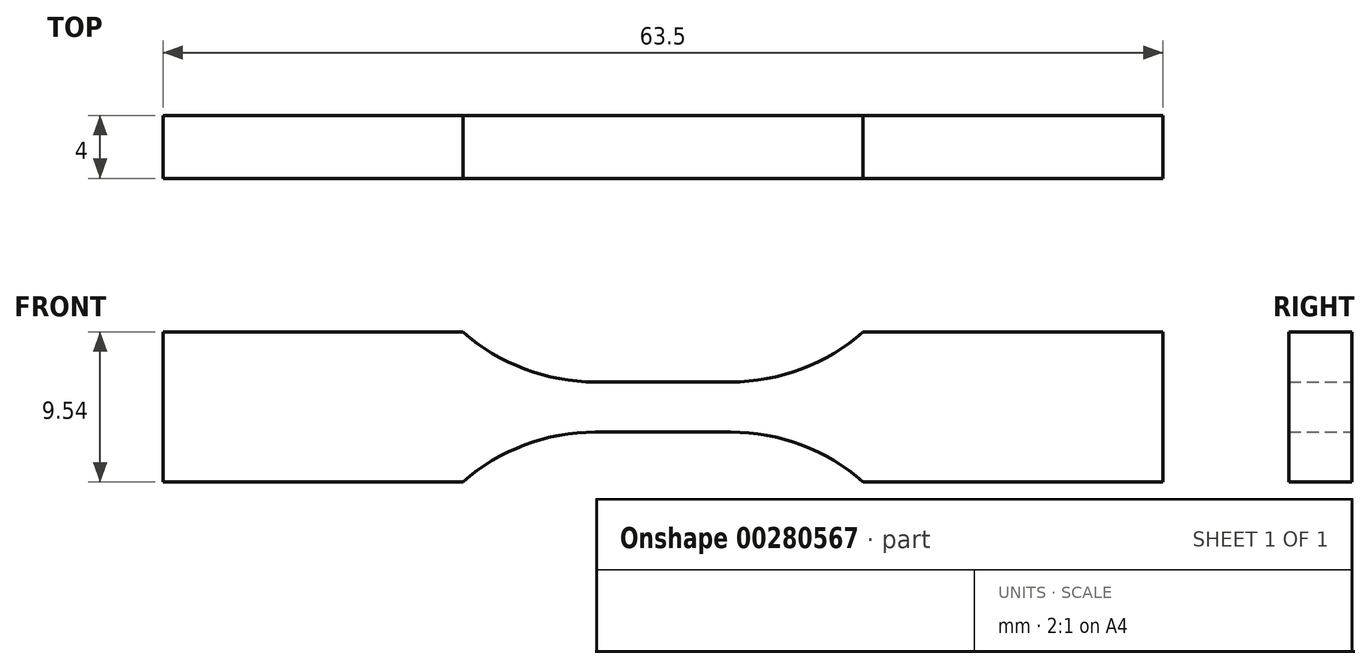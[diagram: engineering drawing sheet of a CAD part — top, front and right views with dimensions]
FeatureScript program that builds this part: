
annotation { "Feature Type Name" : "Feature", "Feature Type Description" : "" }
export const myFeature = defineFeature(function(context is Context, id is Id, definition is map)
    precondition{}
    {
        {
            var Q0;
            Q0=qCreatedBy(makeId("Front.planeOp"),FACE);
            var sketch = newSketch(context, id + "F0", { "sketchPlane" : qUnion([Q0])});
            skLineSegment(sketch, "E0", {"start": v(0, 1.6) * mm, "end": v(4.3, 1.6) * mm});
            skArc(sketch, "E1", {"start": v(4.3, 1.6) * mm, "mid": v(8.79, 2.41) * mm, "end": v(12.7, 4.76) * mm});
            skLineSegment(sketch, "E2", {"start": v(12.7, 4.77) * mm, "end": v(31.75, 4.77) * mm});
            skLineSegment(sketch, "E3", {"start": v(31.75, 4.77) * mm, "end": v(31.75, 0) * mm});
            skLineSegment(sketch, "E4.MirrorCS", {"start": v(0, -1.6) * mm, "end": v(4.3, -1.6) * mm});
            skLineSegment(sketch, "E5.MirrorCS", {"start": v(31.75, -4.77) * mm, "end": v(31.75, 0) * mm});
            skLineSegment(sketch, "E6.MirrorCS", {"start": v(12.7, -4.77) * mm, "end": v(31.75, -4.77) * mm});
            skArc(sketch, "E7.MirrorCS", {"start": v(4.3, -1.6) * mm, "mid": v(8.79, -2.41) * mm, "end": v(12.7, -4.76) * mm});
            skArc(sketch, "E8.MirrorCS", {"start": v(-4.3, -1.6) * mm, "mid": v(-8.79, -2.41) * mm, "end": v(-12.7, -4.76) * mm});
            skLineSegment(sketch, "E9.MirrorCS", {"start": v(-12.7, -4.77) * mm, "end": v(-31.75, -4.77) * mm});
            skArc(sketch, "E10.MirrorCS", {"start": v(-4.3, 1.6) * mm, "mid": v(-8.79, 2.41) * mm, "end": v(-12.7, 4.76) * mm});
            skLineSegment(sketch, "E11.MirrorCS", {"start": v(-12.7, 4.77) * mm, "end": v(-31.75, 4.77) * mm});
            skLineSegment(sketch, "E12.MirrorCS", {"start": v(-31.75, -4.77) * mm, "end": v(-31.75, 0) * mm});
            skLineSegment(sketch, "E13.MirrorCS", {"start": v(0, -1.59) * mm, "end": v(-4.3, -1.59) * mm});
            skLineSegment(sketch, "E14.MirrorCS", {"start": v(-31.75, 4.77) * mm, "end": v(-31.75, 0) * mm});
            skLineSegment(sketch, "E15.MirrorCS", {"start": v(0, 1.6) * mm, "end": v(-4.3, 1.6) * mm});
            skSolve(sketch);
        }
        {
            var Q0;
            Q0 = qSketchRegion(id + "F0", true);
            extrude(context, id + "F1", {"entities" : qUnion([Q0]), "endBound" : BoundingType.SYMMETRIC, "depth" : 4 * mm});
        }
    });
